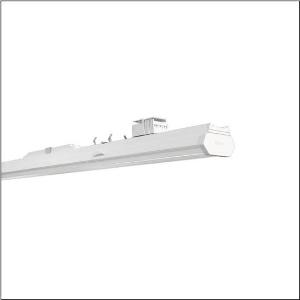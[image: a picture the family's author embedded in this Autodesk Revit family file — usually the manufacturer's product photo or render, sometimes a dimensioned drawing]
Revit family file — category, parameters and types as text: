
# Revit family: licross_r__11_protected_mo_51tp11dn695g_68fa
name_source: partatom
category: Lighting Fixtures
units: mm (PartAtom-declared; Revit-internal decimal feet)

## family parameters
Cut with Voids When Loaded = No
Host = Face
Light Source = No
Part Type = Normal
Room Calculation Point = No
Round Connector Dimension = Use Diameter
Shared = No

## types (1)
- --- (1 x LED, 9680 lm, 57.1 W, 6500K)
    Apparent Load = 57 VA
    CIE Flux Codes = 83 94 98 100 100
    Color Rendering = 80
    Color Temperature = 6500K
    Default Elevation = 1800 mm
    Description = Licross® 11 Protected MO, luminaire insert, of sheet steel, galvanised, coil coated, white, length: 1.500mm, width: 90mm, height: 101mm, LED rated luminous flux: 9.680lm, light colour: 865, control gear: DALI 2, with plug, 5-pole, with phase selection, mains connection: 220..240V, AC, 50/60Hz, rated input power: 57W, halogen-free wiring, primary light control with lens, of plastic, primary optical cover: cover, of PMMA, light emission: direct distribution, primary light characteristic: symmetric, protection rating (complete): IP64, insulation class (complete): insulation class I (protective earthing), certification: CE, ENEC, VDE, UKCA, protection symbol: D if used in an environment with conductive dust loads with corresponding accessories, impact resistance: IK06, permissible ambient temperature for indoor applications: -25..+35°C, corresponds to IFS (International Featured Standards) requirements for safety and quality in the food industry, reducing of maximum allowable ambient temperature of 5°C with ceiling mounting, LABS conformity tested according to VDMA 24364:2018-05, packaging unit: 1 piece
    Height = 92 mm
    Lamp = 1 x LED
    Lamp Light Flux = 9680 lm
    Lamp Power = 57.1 W
    Lamp count = 1
    Length = 1500 mm
    Luminous efficacy = 170 lm/W
    Manufacturer = Siteco
    ModVariant = No
    Model = 51TP11DN695G
    Mounting Place = Ceiling
    Mounting Type = Pendant
    Number of Poles = 1
    OnlyDefault = Yes
    Power Factor = 1
    Product Name = Licross® 11 Protected MO
    Product group = luminaire insert
    ProductGroupID = 901
    Protection Class = Protection class I
    Protection Degree = IP 64
    RLX_Detail_Level = 1
    RLX_Emergency_Light_Flux = 0 lm
    RLX_Emergency_Type = 0
    RLX_Emergency_Type_DB = No
    RlxData = <blob elided: 24089 chars, md5=09ff204d>
    Socket = socket
    Standby Power = 0 W
    System Light Flux = 9680 lm
    System Power = 57 W
    Type Comments = factory setting: luminous flux: 100 % | dim-lin: 254 | 378 mA
    Type Image = l_1256148.jpg
    URL = http://relux.com
    VarID = @adj_006779
    Voltage = 0 V
    Weight = 0.00 kg
    Width = 88 mm

## geometry (parser evidence)
native form markers: Blend x4, Sweep x10
no freeform markers — native parametric forms only
